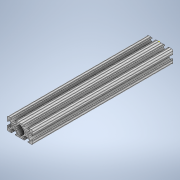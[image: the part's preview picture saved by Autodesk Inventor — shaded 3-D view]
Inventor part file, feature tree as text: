
AUTODESK INVENTOR PART (.ipt)
format: ipt  version: 2020 (Build 240168000, 168)  size: 333,824 bytes
history: native  units: in
note: dims shown in document units (in); Inventor stores cm internally (conversion verified against a paired STEP export)
features: sketch x2, extrude x1
ambient origin geometry x8: Origin, YZ Plane, XZ Plane, XY Plane, X Axis, Y Axis, Z Axis, Center Point
bodies: Solid1 (feature_tree)
feature tree (3):
  extrude  "Extrusion1"  [1 undecoded]
  sketch  "Sketch2"
  sketch  "Sketch1"  dims[d0=11.0in d1=0.0in]
note: 1 required parameter value undecoded (feature->parameter linkage not recoverable at this tier; creation-order binding heuristic only, values carry confidence <= 0.55)
